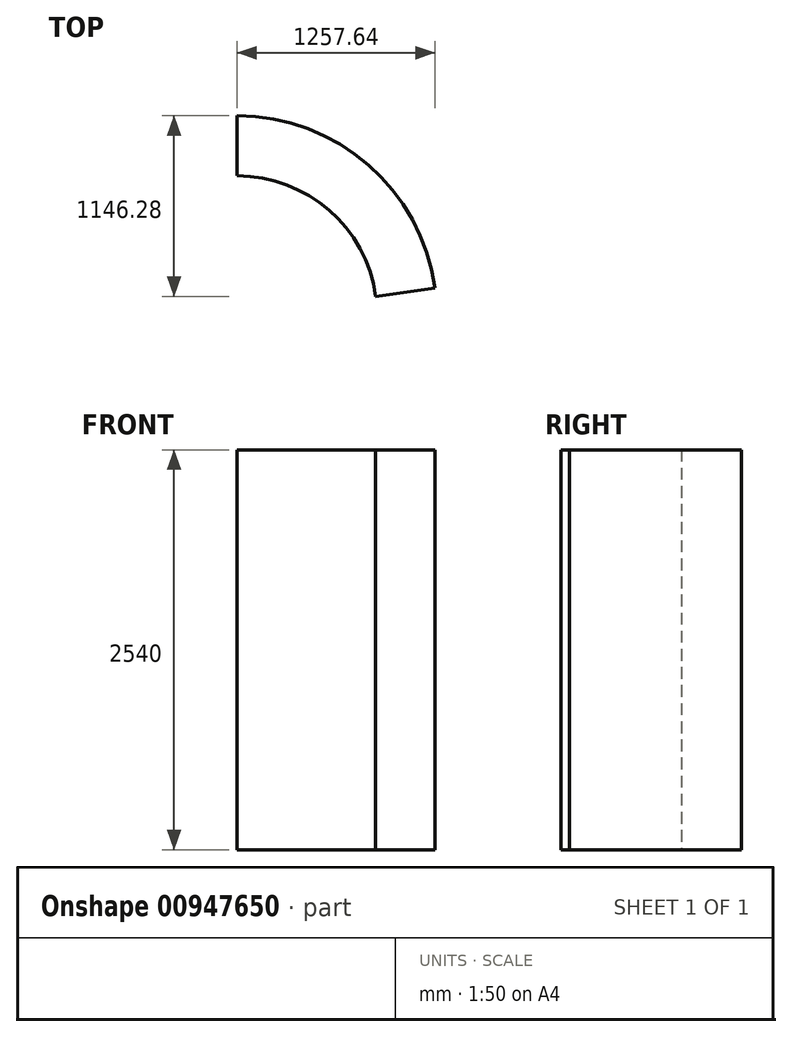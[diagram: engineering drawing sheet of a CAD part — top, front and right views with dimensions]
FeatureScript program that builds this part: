
annotation { "Feature Type Name" : "Feature", "Feature Type Description" : "" }
export const myFeature = defineFeature(function(context is Context, id is Id, definition is map)
    precondition{}
    {
        {
            var Q0;
            Q0=qCreatedBy(makeId("Top.planeOp"),FACE);
            var sketch = newSketch(context, id + "F0", { "sketchPlane" : qUnion([Q0])});
            skCircle(sketch, "E0", {"center": v(0, 0) * mm, "radius": 1270 * mm});
            skCircle(sketch, "E1", {"center": v(0, 0) * mm, "radius": 889 * mm});
            skSolve(sketch);
        }
        {
            var Q0;
            Q0=qCreatedBy(makeId("Top.planeOp"),FACE);
            var sketch = newSketch(context, id + "F1", { "sketchPlane" : qUnion([Q0])});
            skLineSegment(sketch, "E2", {"start": v(880.35, 123.72) * mm, "end": v(1257.64, 176.75) * mm});
            skArc(sketch, "E3.0", {"start": v(1257.64, 176.75) * mm, "mid": v(833.2, 958.48) * mm, "end": v(0, 1270) * mm});
            skArc(sketch, "E4.0", {"start": v(880.35, 123.72) * mm, "mid": v(583.24, 670.94) * mm, "end": v(0, 889) * mm});
            skLineSegment(sketch, "E5", {"start": v(0, 1270) * mm, "end": v(0, 889) * mm});
            skSolve(sketch);
        }
        {
            var Q0;
            Q0 = qSketchRegion(id + "F1", true);
            extrude(context, id + "F2", {"entities" : qUnion([Q0]), "depth" : 2540 * mm, "offsetDistance" : 25.4 * mm});
        }
    });
